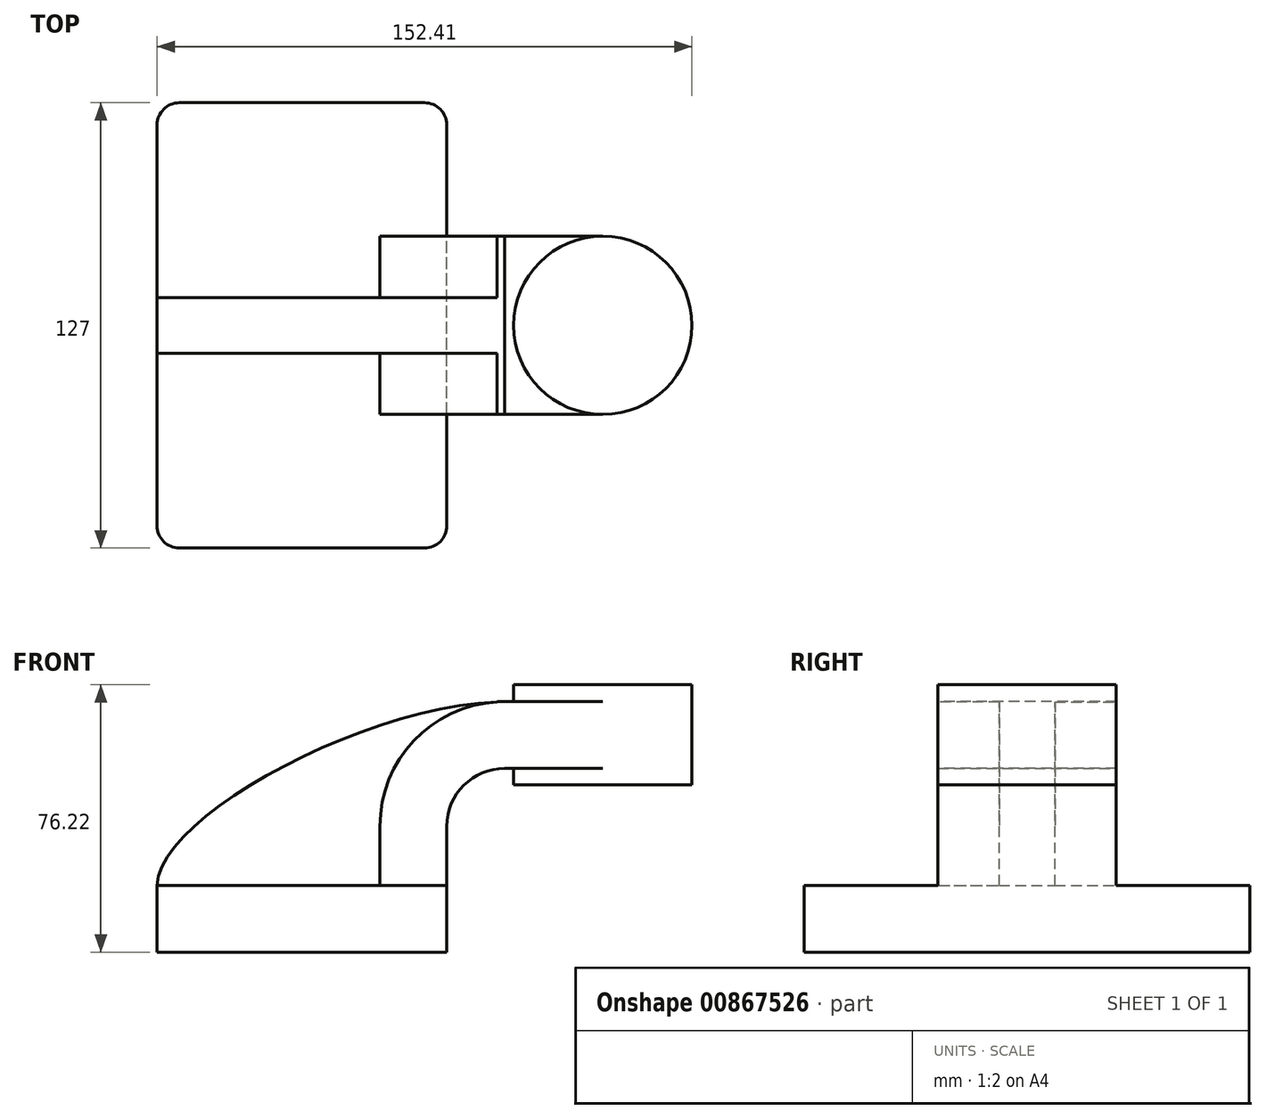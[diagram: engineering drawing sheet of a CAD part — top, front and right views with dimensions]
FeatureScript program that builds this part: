
annotation { "Feature Type Name" : "Feature", "Feature Type Description" : "" }
export const myFeature = defineFeature(function(context is Context, id is Id, definition is map)
    precondition{}
    {
        {
            var Q0;
            Q0=qCreatedBy(makeId("Front.planeOp"),FACE);
            var sketch = newSketch(context, id + "F0", { "sketchPlane" : qUnion([Q0])});
            skLineSegment(sketch, "E0.bottom", {"start": v(-41.28, -9.53) * mm, "end": v(41.28, -9.53) * mm});
            skLineSegment(sketch, "E0.top", {"start": v(-41.28, 9.53) * mm, "end": v(41.28, 9.53) * mm});
            skLineSegment(sketch, "E0.left", {"start": v(-41.28, -9.53) * mm, "end": v(-41.28, 9.53) * mm});
            skLineSegment(sketch, "E0.right", {"start": v(41.28, -9.53) * mm, "end": v(41.28, 9.53) * mm});
            skPoint(sketch, "E0.middle", {"position": v(0, 0) * mm});
            skLineSegment(sketch, "E1", {"start": v(41.28, 9.53) * mm, "end": v(41.28, 26.37) * mm});
            skArc(sketch, "E2", {"start": v(41.27, 26.37) * mm, "mid": v(46.11, 38.04) * mm, "end": v(57.78, 42.88) * mm});
            skLineSegment(sketch, "E3", {"start": v(57.78, 42.88) * mm, "end": v(85.72, 42.88) * mm});
            skLineSegment(sketch, "E4.0", {"start": v(57.78, 61.93) * mm, "end": v(85.72, 61.93) * mm});
            skArc(sketch, "E4.1", {"start": v(22.22, 26.37) * mm, "mid": v(32.64, 51.5) * mm, "end": v(57.78, 61.93) * mm});
            skLineSegment(sketch, "E4.2", {"start": v(22.22, 9.53) * mm, "end": v(22.22, 26.37) * mm});
            skLineSegment(sketch, "E5", {"start": v(85.72, 61.93) * mm, "end": v(85.72, 42.88) * mm});
            skLineSegment(sketch, "E6.bottom", {"start": v(60.33, 66.69) * mm, "end": v(111.12, 66.69) * mm});
            skLineSegment(sketch, "E6.top", {"start": v(60.32, 38.11) * mm, "end": v(111.12, 38.11) * mm});
            skLineSegment(sketch, "E6.left", {"start": v(60.32, 66.69) * mm, "end": v(60.32, 38.11) * mm});
            skLineSegment(sketch, "E6.right", {"start": v(111.12, 66.69) * mm, "end": v(111.12, 38.11) * mm});
            skPoint(sketch, "E6.middle", {"position": v(85.72, 52.4) * mm});
            skLineSegment(sketch, "E7", {"start": v(85.72, 42.88) * mm, "end": v(85.72, 38.11) * mm});
            skFitSpline(sketch, "E8", {"points": [v(-41.28, 9.52) * mm, v(57.79, 61.93) * mm], "startDerivative": vector(1.01, 58.64) * mm, "endDerivative": vector(118.6, 2) * mm});
            skLineSegment(sketch, "E9", {"start": v(85.72, 61.93) * mm, "end": v(85.72, 66.69) * mm});
            skSolve(sketch);
        }
        {
            var Q0;
            Q0=makeQuery(id+"F0.imprint","IMPRINT",FACE,{"disambiguationData":[TD([[makeQuery(id+"F0.imprint","IMPRINT",EDGE,{"derivedFrom":sQuery(id+"F0.wireOp",EDGE,"E0.bottom")}),1.0]])]});
            extrude(context, id + "F1", {"entities" : qUnion([Q0]), "endBound" : BoundingType.SYMMETRIC, "depth" : 127 * mm, "offsetDistance" : 25.4 * mm});
        }
        {
            var Q0;
            {var subQ1=sQuery(id+"F0.wireOp",EDGE,"E1");Q0=makeQuery(id+"F0.imprint","IMPRINT",FACE,{"disambiguationData":[TD([[makeQuery(id+"F0.imprint","IMPRINT",EDGE,{"derivedFrom":subQ1}),1.0]])]});}
            var Q1;
            {var subQ0=sQuery(id+"F0.wireOp",EDGE,"E5");Q1=makeQuery(id+"F0.imprint","IMPRINT",FACE,{"disambiguationData":[TD([[makeQuery(id+"F0.imprint","IMPRINT",EDGE,{"derivedFrom":subQ0}),-1.0]])]});}
            extrude(context, id + "F2", {"entities" : qUnion([Q0, Q1]), "operationType" : NewBodyOperationType.ADD, "endBound" : BoundingType.SYMMETRIC, "depth" : 50.8 * mm, "offsetDistance" : 25.4 * mm});
        }
        {
            var Q0;
            {var subQ3=sQuery(id+"F0.wireOp",EDGE,"E4.2");Q0=makeQuery(id+"F0.imprint","IMPRINT",FACE,{"disambiguationData":[TD([[makeQuery(id+"F0.imprint","IMPRINT",EDGE,{"derivedFrom":subQ3}),1.0]])]});}
            extrude(context, id + "F3", {"entities" : qUnion([Q0]), "operationType" : NewBodyOperationType.ADD, "endBound" : BoundingType.SYMMETRIC, "depth" : 15.88 * mm, "offsetDistance" : 25.4 * mm});
        }
        {
            var Q0;
            Q0=makeQuery(id+"F0.imprint","IMPRINT",FACE,{"disambiguationData":[TD([[makeQuery(id+"F0.imprint","IMPRINT",EDGE,{"derivedFrom":sQuery(id+"F0.wireOp",EDGE,"E5")}),1.0]])]});
            var Q1;
            Q1=sQuery(id+"F0.wireOp",EDGE,"E5");
            revolve(context, id + "F4", {"operationType" : NewBodyOperationType.ADD, "surfaceOperationType" : NewSurfaceOperationType.NEW, "entities" : qUnion([Q0]), "axis" : qUnion([Q1]), "revolveType" : RevolveType.FULL});
        }
        {
            var Q0;
            Q0=makeQuery(id+"F1.opExtrude","CAP_EDGE",EDGE,{"disambiguationData":[OSD([sQuery(id+"F0.wireOp",EDGE,"E0.right")])],"isStart":true});
            var Q1;
            Q1=makeQuery(id+"F1.opExtrude","CAP_EDGE",EDGE,{"disambiguationData":[OSD([sQuery(id+"F0.wireOp",EDGE,"E0.left")])],"isStart":true});
            var Q2;
            Q2=makeQuery(id+"F1.opExtrude","CAP_EDGE",EDGE,{"disambiguationData":[OSD([sQuery(id+"F0.wireOp",EDGE,"E0.left")])],"isStart":false});
            var Q3;
            Q3=makeQuery(id+"F1.opExtrude","CAP_EDGE",EDGE,{"disambiguationData":[OSD([sQuery(id+"F0.wireOp",EDGE,"E0.right")])],"isStart":false});
            fillet(context, id + "F5", {"entities" : qUnion([Q0, Q1, Q2, Q3]), "radius" : 6.35 * mm, "tangentPropagation" : true, "allowEdgeOverflow" : false});
        }
    });
